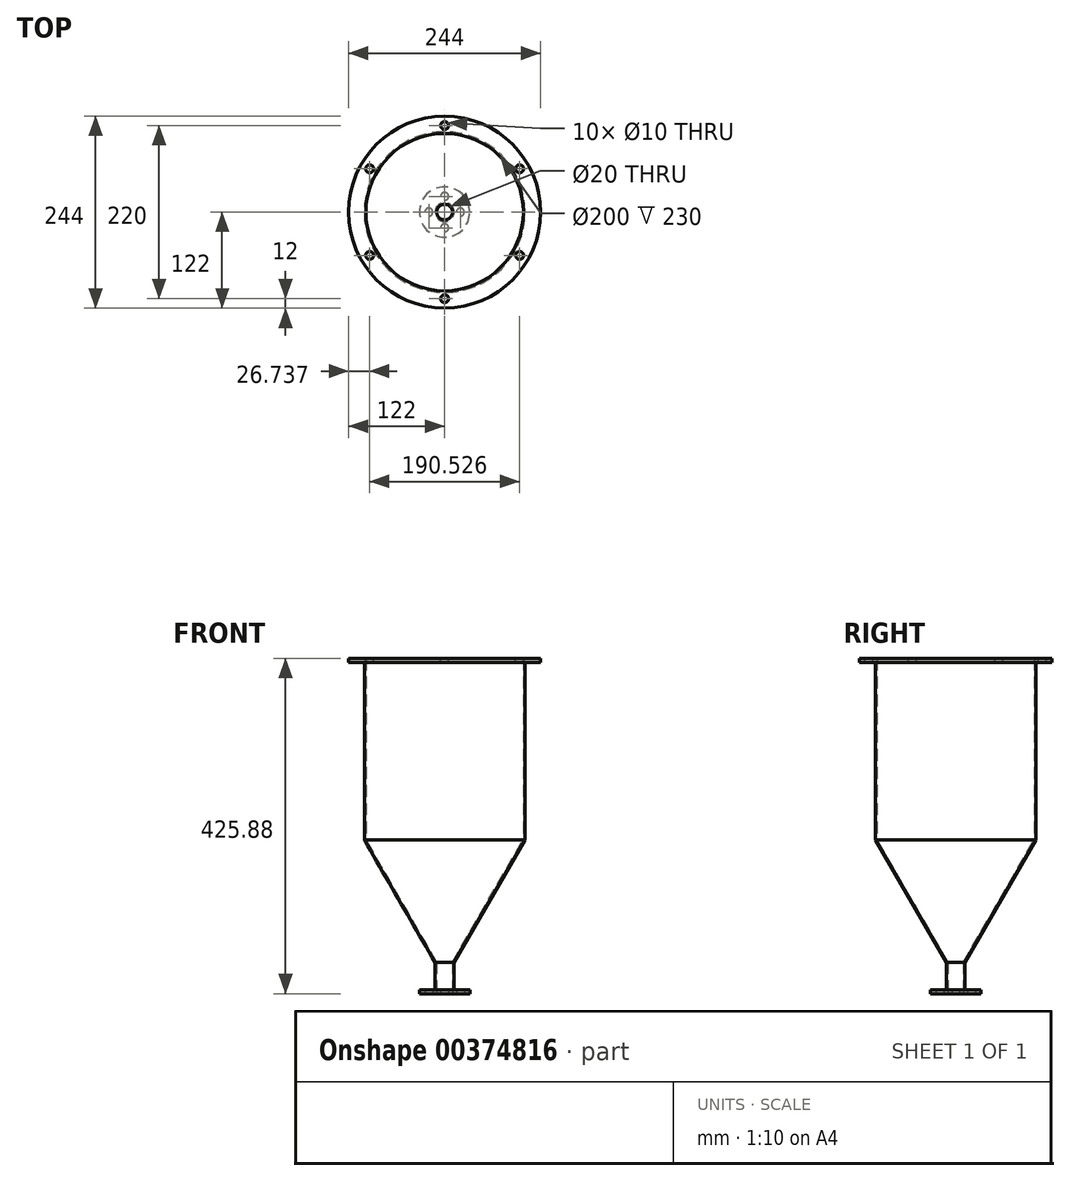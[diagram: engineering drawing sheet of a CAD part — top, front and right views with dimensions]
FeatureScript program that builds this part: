
annotation { "Feature Type Name" : "Feature", "Feature Type Description" : "" }
export const myFeature = defineFeature(function(context is Context, id is Id, definition is map)
    precondition{}
    {
        {
            var Q0;
            Q0=qCreatedBy(makeId("Front.planeOp"),FACE);
            var sketch = newSketch(context, id + "F0", { "sketchPlane" : qUnion([Q0])});
            skLineSegment(sketch, "E0", {"start": v(-100, 425.88) * mm, "end": v(-100, 195.88) * mm});
            skLineSegment(sketch, "E1", {"start": v(-100, 195.88) * mm, "end": v(-10, 40) * mm});
            skLineSegment(sketch, "E2", {"start": v(-10, 40) * mm, "end": v(-10, 0) * mm});
            skLineSegment(sketch, "E3", {"start": v(0, 0) * mm, "end": v(0, 425.88) * mm, "construction": true});
            skLineSegment(sketch, "E4.0", {"start": v(-12, 39.46) * mm, "end": v(-12, 0) * mm});
            skLineSegment(sketch, "E4.1", {"start": v(-102, 195.35) * mm, "end": v(-12, 39.46) * mm});
            skLineSegment(sketch, "E4.2", {"start": v(-102, 425.88) * mm, "end": v(-102, 195.35) * mm});
            skLineSegment(sketch, "E5", {"start": v(-102, 425.88) * mm, "end": v(-100, 425.88) * mm});
            skLineSegment(sketch, "E6", {"start": v(-12, 0) * mm, "end": v(-10, 0) * mm});
            skSolve(sketch);
        }
        {
            var Q0;
            Q0=makeQuery(id+"F0.imprint","IMPRINT",FACE,{"disambiguationData":[TD([[makeQuery(id+"F0.imprint","IMPRINT",EDGE,{"derivedFrom":sQuery(id+"F0.wireOp",EDGE,"E0")}),-1.0]])]});
            var Q1;
            Q1=sQuery(id+"F0.wireOp",EDGE,"E3");
            revolve(context, id + "F1", {"entities" : qUnion([Q0]), "axis" : qUnion([Q1]), "revolveType" : RevolveType.FULL});
        }
        {
            var Q0;
            Q0=makeQuery(id+"F1.opRevolve","SWEPT_FACE",FACE,{"disambiguationData":[OSD([sQuery(id+"F0.wireOp",EDGE,"E5")])]});
            var sketch = newSketch(context, id + "F2", { "sketchPlane" : qUnion([Q0])});
            skCircle(sketch, "E7", {"center": v(0, 0) * mm, "radius": 122 * mm});
            skSolve(sketch);
        }
        {
            var Q0;
            Q0=makeQuery(id+"F2.imprint","IMPRINT",FACE,{"disambiguationData":[TD([[makeQuery(id+"F2.imprint","IMPRINT",EDGE,{"derivedFrom":sQuery(id+"F2.wireOp",EDGE,"E7")}),1.0]])]});
            extrude(context, id + "F3", {"entities" : qUnion([Q0]), "operationType" : NewBodyOperationType.ADD, "oppositeDirection" : true, "depth" : 5 * mm});
        }
        {
            var Q0;
            Q0=makeQuery(id+"F1.opRevolve","SWEPT_FACE",FACE,{"disambiguationData":[OSD([sQuery(id+"F0.wireOp",EDGE,"E6")])]});
            var sketch = newSketch(context, id + "F4", { "sketchPlane" : qUnion([Q0])});
            skCircle(sketch, "E8", {"center": v(0, 0) * mm, "radius": 32 * mm});
            skSolve(sketch);
        }
        {
            var Q0;
            Q0=makeQuery(id+"F4.imprint","IMPRINT",FACE,{"disambiguationData":[TD([[makeQuery(id+"F4.imprint","IMPRINT",EDGE,{"derivedFrom":sQuery(id+"F4.wireOp",EDGE,"E8")}),1.0]])]});
            extrude(context, id + "F5", {"entities" : qUnion([Q0]), "operationType" : NewBodyOperationType.ADD, "oppositeDirection" : true, "offsetDistance" : 25 * mm, "depth" : 5 * mm});
        }
        {
            var Q0;
            {var subQ0=sQuery(id+"F0.wireOp",EDGE,"E5");Q0=makeQuery(id+"F3.boolean.opBoolean","MERGE",FACE,{"derivedFrom":[makeQuery(id+"F1.opRevolve","SWEPT_FACE",FACE,{"disambiguationData":[OSD([subQ0])]}),makeQuery(id+"F3.opExtrude","CAP_FACE",FACE,{"disambiguationData":[OSD([sQuery(id+"F0.wireOp",EDGE,"E4.2"),subQ0,sQuery(id+"F2.wireOp",EDGE,"E7")])],"isStart":true})]});}
            var sketch = newSketch(context, id + "F6", { "sketchPlane" : qUnion([Q0])});
            skCircle(sketch, "E9", {"center": v(0, 110) * mm, "radius": 5 * mm});
            skCircle(sketch, "E10.1.0", {"center": v(-95.26, 55) * mm, "radius": 5 * mm});
            skCircle(sketch, "E10.2.0", {"center": v(-95.26, -55) * mm, "radius": 5 * mm});
            skPoint(sketch, "E10.center", {"position": v(0, 0) * mm});
            skCircle(sketch, "E11.1.3.0", {"center": v(0, -110) * mm, "radius": 5 * mm});
            skCircle(sketch, "E11.1.4.0", {"center": v(95.26, -55) * mm, "radius": 5 * mm});
            skCircle(sketch, "E11.1.5.0", {"center": v(95.26, 55) * mm, "radius": 5 * mm});
            skSolve(sketch);
        }
        {
            var Q0;
            Q0 = qSketchRegion(id + "F6", true);
            extrude(context, id + "F7", {"entities" : qUnion([Q0]), "operationType" : NewBodyOperationType.REMOVE, "endBound" : BoundingType.THROUGH_ALL, "oppositeDirection" : true, "depth" : 25 * mm});
        }
        {
            var Q0;
            {var subQ0=sQuery(id+"F0.wireOp",EDGE,"E6");Q0=makeQuery(id+"F5.boolean.opBoolean","MERGE",FACE,{"derivedFrom":[makeQuery(id+"F1.opRevolve","SWEPT_FACE",FACE,{"disambiguationData":[OSD([subQ0])]}),makeQuery(id+"F5.opExtrude","CAP_FACE",FACE,{"disambiguationData":[OSD([sQuery(id+"F0.wireOp",EDGE,"E4.0"),subQ0,sQuery(id+"F4.wireOp",EDGE,"E8")])],"isStart":true})]});}
            var sketch = newSketch(context, id + "F8", { "sketchPlane" : qUnion([Q0])});
            skCircle(sketch, "E12", {"center": v(0, 20) * mm, "radius": 5 * mm});
            skCircle(sketch, "E13.1.0", {"center": v(-20, 0) * mm, "radius": 5 * mm});
            skCircle(sketch, "E13.2.0", {"center": v(0, -20) * mm, "radius": 5 * mm});
            skPoint(sketch, "E13.center", {"position": v(0, 0) * mm});
            skCircle(sketch, "E14.1.3.0", {"center": v(20, 0) * mm, "radius": 5 * mm});
            skSolve(sketch);
        }
        {
            var Q0;
            Q0 = qSketchRegion(id + "F8", true);
            var Q1;
            Q1=makeQuery(id+"F5.opExtrude","CAP_FACE",FACE,{"disambiguationData":[OSD([sQuery(id+"F0.wireOp",EDGE,"E4.0"),sQuery(id+"F0.wireOp",EDGE,"E6"),sQuery(id+"F4.wireOp",EDGE,"E8")])],"isStart":false});
            extrude(context, id + "F9", {"entities" : qUnion([Q0]), "operationType" : NewBodyOperationType.REMOVE, "endBound" : BoundingType.UP_TO_SURFACE, "oppositeDirection" : true, "endBoundEntityFace" : qUnion([Q1]), "depth" : 25 * mm});
        }
    });
